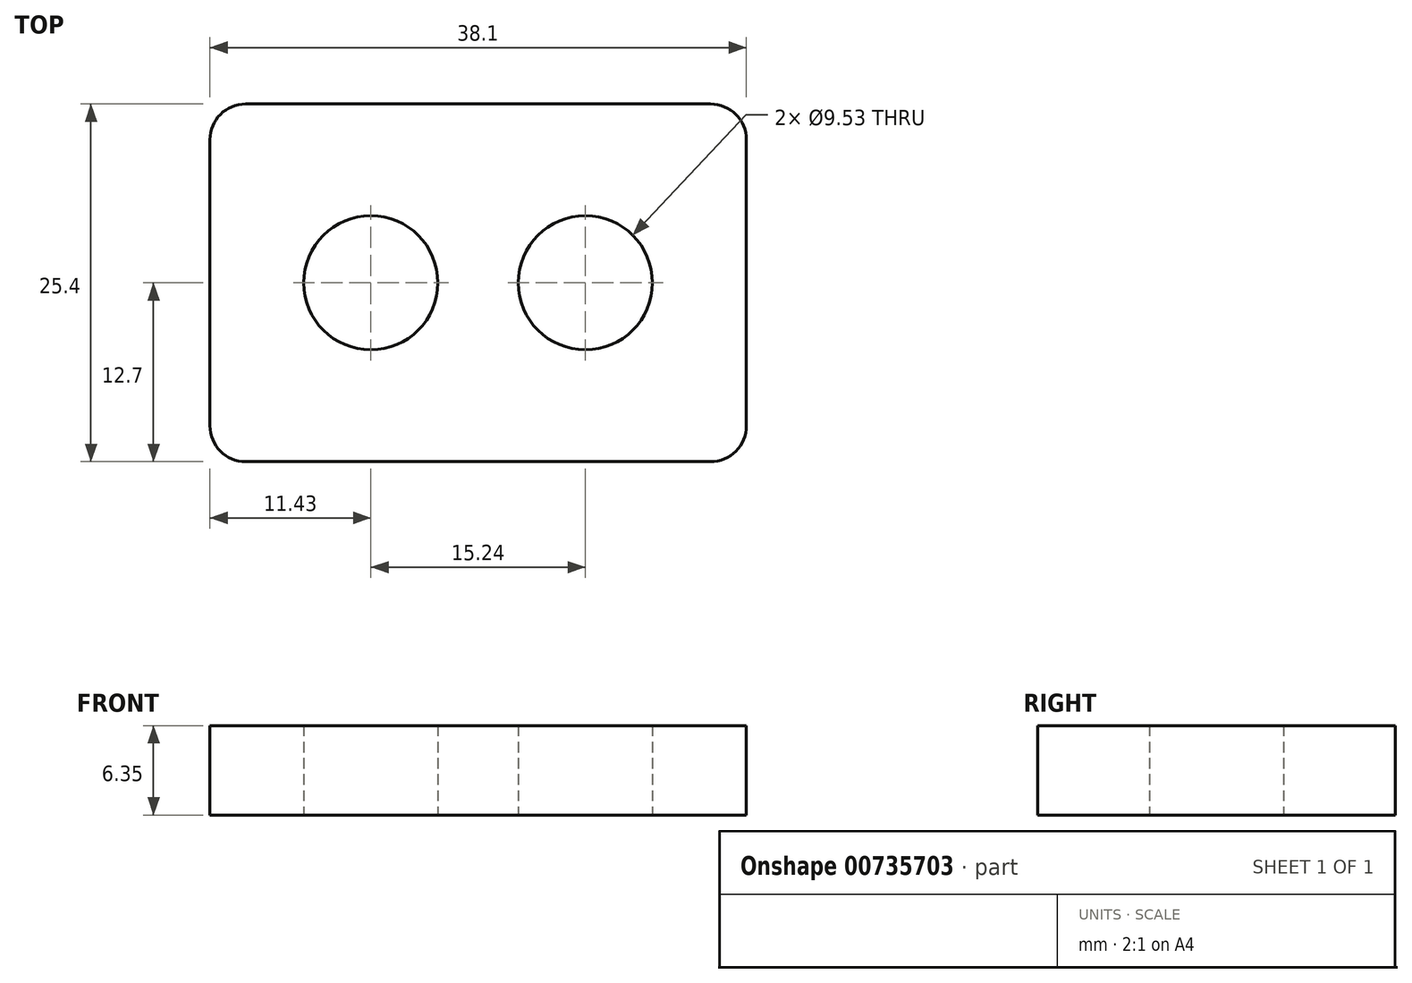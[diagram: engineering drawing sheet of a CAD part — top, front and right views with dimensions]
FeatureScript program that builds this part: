
annotation { "Feature Type Name" : "Feature", "Feature Type Description" : "" }
export const myFeature = defineFeature(function(context is Context, id is Id, definition is map)
    precondition{}
    {
        {
            var Q0;
            Q0=qCreatedBy(makeId("Top.planeOp"),FACE);
            var sketch = newSketch(context, id + "F0", { "sketchPlane" : qUnion([Q0])});
            skLineSegment(sketch, "E0.bottom", {"start": v(2.54, 0) * mm, "end": v(35.56, 0) * mm});
            skLineSegment(sketch, "E0.top", {"start": v(2.54, 25.4) * mm, "end": v(35.56, 25.4) * mm});
            skLineSegment(sketch, "E0.left", {"start": v(0, 2.54) * mm, "end": v(0, 22.86) * mm});
            skLineSegment(sketch, "E0.right", {"start": v(38.1, 2.54) * mm, "end": v(38.1, 22.86) * mm});
            skPoint(sketch, "E1.visualSharp", {"position": v(0, 25.4) * mm});
            skArc(sketch, "E1.filletArc", {"start": v(2.54, 25.4) * mm, "mid": v(0.74, 24.66) * mm, "end": v(0, 22.86) * mm});
            skPoint(sketch, "E2.visualSharp", {"position": v(0, 0) * mm});
            skArc(sketch, "E2.filletArc", {"start": v(0, 2.54) * mm, "mid": v(0.74, 0.74) * mm, "end": v(2.54, 0) * mm});
            skPoint(sketch, "E3.visualSharp", {"position": v(38.1, 25.4) * mm});
            skArc(sketch, "E3.filletArc", {"start": v(38.1, 22.86) * mm, "mid": v(37.36, 24.66) * mm, "end": v(35.56, 25.4) * mm});
            skPoint(sketch, "E4.visualSharp", {"position": v(38.1, 0) * mm});
            skArc(sketch, "E4.filletArc", {"start": v(35.56, 0) * mm, "mid": v(37.36, 0.74) * mm, "end": v(38.1, 2.54) * mm});
            skPoint(sketch, "E5", {"position": v(11.43, 12.7) * mm});
            skPoint(sketch, "E5.positionSnap0", {"position": v(0, 12.7) * mm});
            skPoint(sketch, "E6", {"position": v(26.67, 12.7) * mm});
            skPoint(sketch, "E6.positionSnap0", {"position": v(38.1, 12.7) * mm});
            skCircle(sketch, "E7", {"center": v(11.43, 12.7) * mm, "radius": 4.76 * mm});
            skCircle(sketch, "E8", {"center": v(26.67, 12.7) * mm, "radius": 4.76 * mm});
            skSolve(sketch);
        }
        {
            var Q0;
            Q0=makeQuery(id+"F0.imprint","IMPRINT",FACE,{"disambiguationData":[TD([[makeQuery(id+"F0.imprint","IMPRINT",EDGE,{"derivedFrom":sQuery(id+"F0.wireOp",EDGE,"E0.bottom")}),1.0]])]});
            extrude(context, id + "F1", {"entities" : qUnion([Q0]), "depth" : 6.35 * mm, "offsetDistance" : 25.4 * mm});
        }
    });
